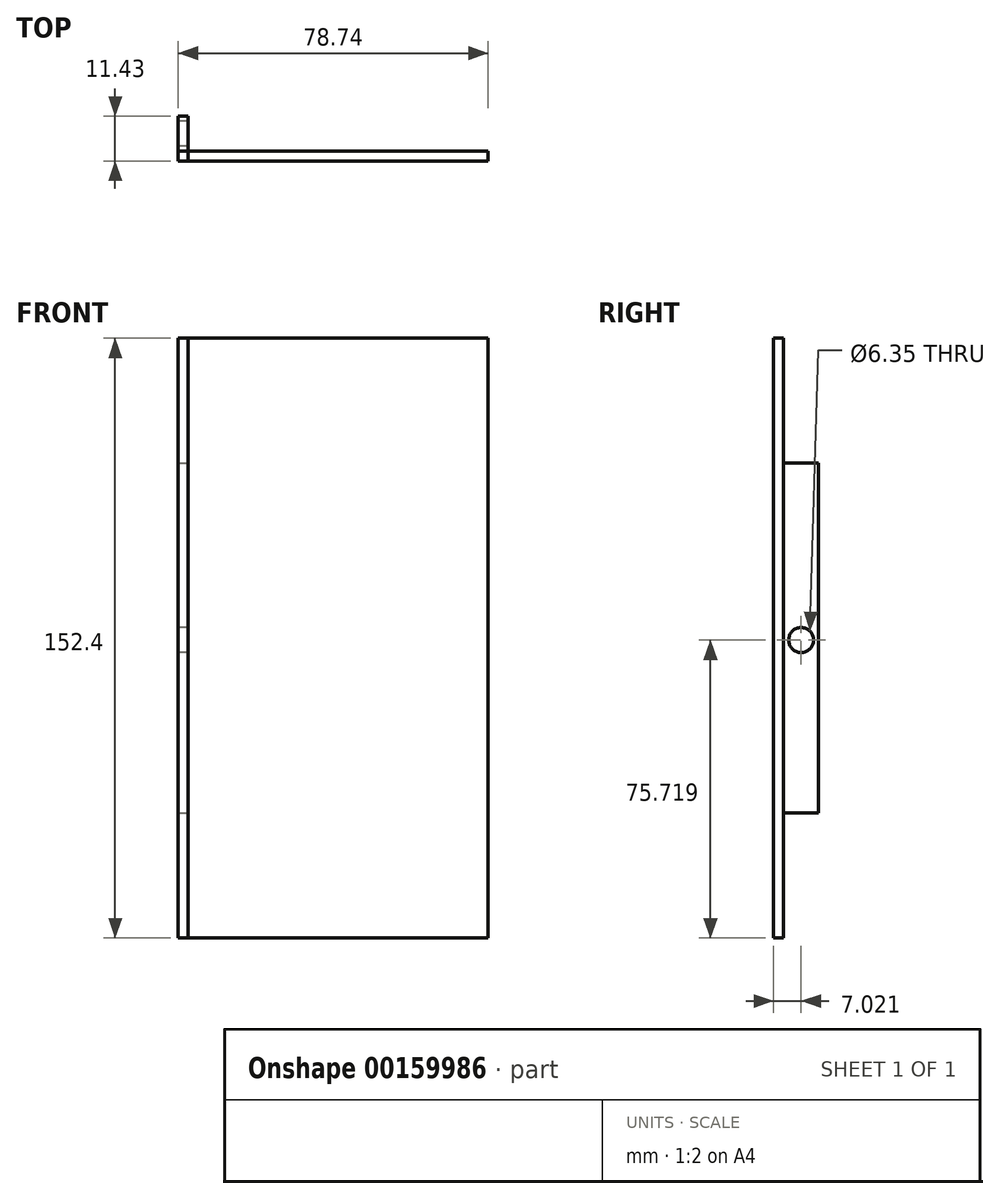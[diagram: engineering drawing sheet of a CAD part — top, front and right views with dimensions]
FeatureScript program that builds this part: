
annotation { "Feature Type Name" : "Feature", "Feature Type Description" : "" }
export const myFeature = defineFeature(function(context is Context, id is Id, definition is map)
    precondition{}
    {
        {
            var Q0;
            Q0=qCreatedBy(makeId("Front.planeOp"),FACE);
            var sketch = newSketch(context, id + "F0", { "sketchPlane" : qUnion([Q0])});
            skLineSegment(sketch, "E0.bottom", {"start": v(0, 0) * mm, "end": v(-76.2, 0) * mm});
            skLineSegment(sketch, "E0.top", {"start": v(0, 152.4) * mm, "end": v(-76.2, 152.4) * mm});
            skLineSegment(sketch, "E0.left", {"start": v(0, 0) * mm, "end": v(0, 152.4) * mm});
            skLineSegment(sketch, "E0.right", {"start": v(-76.2, 0) * mm, "end": v(-76.2, 152.4) * mm});
            skSolve(sketch);
        }
        {
            var Q0;
            Q0=makeQuery(id+"F0.imprint","IMPRINT",FACE,{"disambiguationData":[TD([[makeQuery(id+"F0.imprint","IMPRINT",EDGE,{"derivedFrom":sQuery(id+"F0.wireOp",EDGE,"E0.bottom")}),-1.0]])]});
            extrude(context, id + "F1", {"entities" : qUnion([Q0]), "depth" : 2.54 * mm});
        }
        {
            var Q0;
            Q0=makeQuery(id+"F1.opExtrude","SWEPT_FACE",FACE,{"disambiguationData":[OSD([sQuery(id+"F0.wireOp",EDGE,"E0.right")])]});
            var sketch = newSketch(context, id + "F2", { "sketchPlane" : qUnion([Q0])});
            skLineSegment(sketch, "E1.bottom", {"start": v(2.54, 31.75) * mm, "end": v(-8.89, 31.75) * mm});
            skLineSegment(sketch, "E1.top", {"start": v(2.54, 120.65) * mm, "end": v(-8.9, 120.65) * mm});
            skLineSegment(sketch, "E1.left", {"start": v(2.54, 31.75) * mm, "end": v(2.54, 120.65) * mm});
            skLineSegment(sketch, "E1.right", {"start": v(-8.89, 31.75) * mm, "end": v(-8.9, 120.65) * mm});
            skLineSegment(sketch, "E2", {"start": v(1.27, 0) * mm, "end": v(1.27, 31.75) * mm});
            skSolve(sketch);
        }
        {
            var Q0;
            {var subQ0=sQuery(id+"F2.wireOp",EDGE,"E1.right");Q0=makeQuery(id+"F2.imprint","IMPRINT",FACE,{"disambiguationData":[TD([[makeQuery(id+"F2.imprint","IMPRINT",EDGE,{"derivedFrom":subQ0}),-1.0]])]});}
            extrude(context, id + "F3", {"entities" : qUnion([Q0]), "depth" : 2.54 * mm});
        }
        {
            var Q0;
            Q0=makeQuery(id+"F1.opExtrude","SWEPT_FACE",FACE,{"disambiguationData":[OSD([sQuery(id+"F0.wireOp",EDGE,"E0.right")])]});
            extrude(context, id + "F4", {"entities" : qUnion([Q0]), "depth" : 2.54 * mm});
        }
        {
            var Q0;
            Q0=makeQuery(id+"F3.opExtrude","CAP_FACE",FACE,{"disambiguationData":[OSD([sQuery(id+"F0.wireOp",EDGE,"E0.right"),sQuery(id+"F2.wireOp",EDGE,"E1.bottom"),sQuery(id+"F2.wireOp",EDGE,"E1.top"),sQuery(id+"F2.wireOp",EDGE,"E1.right")])],"isStart":false});
            var sketch = newSketch(context, id + "F5", { "sketchPlane" : qUnion([Q0])});
            skCircle(sketch, "E3", {"center": v(-4.48, 75.72) * mm, "radius": 3.18 * mm});
            skSolve(sketch);
        }
        {
            var Q0;
            Q0=sQuery(id+"F5.wireOp",VERTEX,"E3.center");
            var Q1;
            Q1=makeQuery(id+"F3.opExtrude","SWEPT_BODY",BODY,{"disambiguationData":[OSD([sQuery(id+"F0.wireOp",EDGE,"E0.right"),sQuery(id+"F2.wireOp",EDGE,"E1.bottom"),sQuery(id+"F2.wireOp",EDGE,"E1.top"),sQuery(id+"F2.wireOp",EDGE,"E1.right")])]});
            hole(context, id + "F6", {"style" : HoleStyle.SIMPLE, "endStyle" : HoleEndStyle.THROUGH, "holeDiameter" : 6.35 * mm, "locations" : qUnion([Q0]), "scope" : qUnion([Q1]), "isTappedThrough" : true});
        }
    });
